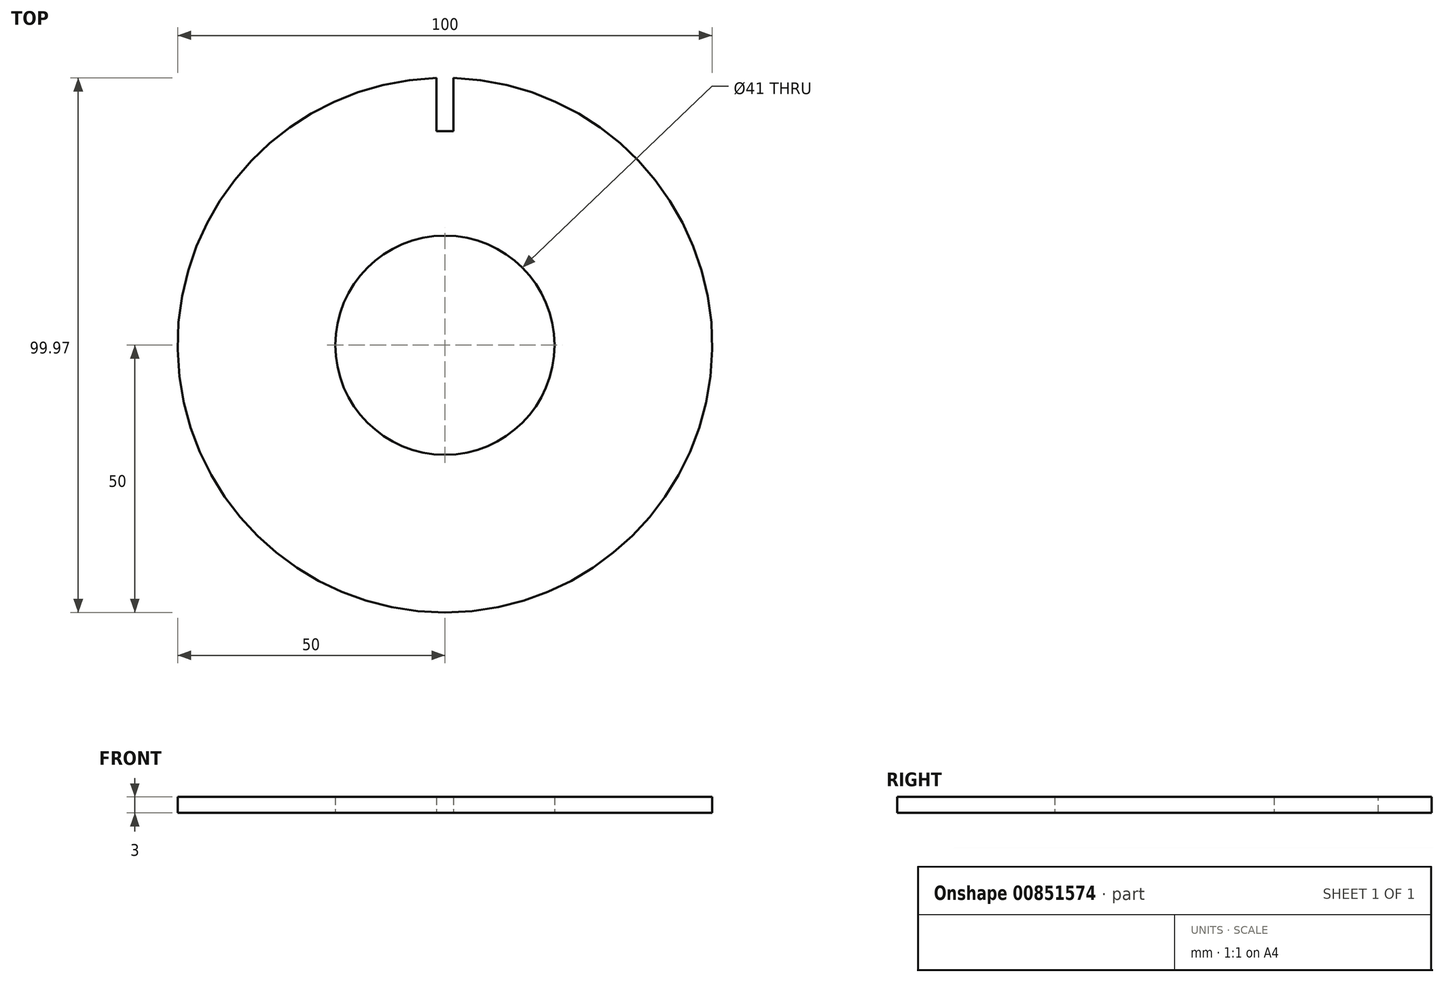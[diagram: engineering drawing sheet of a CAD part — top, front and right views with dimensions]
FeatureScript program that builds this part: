
annotation { "Feature Type Name" : "Feature", "Feature Type Description" : "" }
export const myFeature = defineFeature(function(context is Context, id is Id, definition is map)
    precondition{}
    {
        {
            var Q0;
            Q0=qCreatedBy(makeId("Top.planeOp"),FACE);
            var sketch = newSketch(context, id + "F0", { "sketchPlane" : qUnion([Q0])});
            skCircle(sketch, "E0", {"center": v(0, 0) * mm, "radius": 50 * mm});
            skCircle(sketch, "E1", {"center": v(0, 0) * mm, "radius": 20.5 * mm});
            skSolve(sketch);
        }
        {
            var Q0;
            Q0=qSketchRegion(id+"F0",true);
            extrude(context, id + "F1", {"entities" : qUnion([Q0]), "depth" : 3 * mm, "offsetDistance" : 25 * mm});
        }
        {
            var Q0;
            Q0=makeQuery(id+"F1.opExtrude","CAP_FACE",FACE,{"disambiguationData":[OSD([sQuery(id+"F0.wireOp",EDGE,"E0"),sQuery(id+"F0.wireOp",EDGE,"E1")])],"isStart":false});
            var sketch = newSketch(context, id + "F2", { "sketchPlane" : qUnion([Q0])});
            skLineSegment(sketch, "E2.bottom", {"start": v(-1.6, 80) * mm, "end": v(1.6, 80) * mm});
            skLineSegment(sketch, "E2.top", {"start": v(-1.6, 40) * mm, "end": v(1.6, 40) * mm});
            skLineSegment(sketch, "E2.left", {"start": v(-1.6, 80) * mm, "end": v(-1.6, 40) * mm});
            skLineSegment(sketch, "E2.right", {"start": v(1.6, 80) * mm, "end": v(1.6, 40) * mm});
            skLineSegment(sketch, "E3", {"start": v(0, 0) * mm, "end": v(0, 51.96) * mm, "construction": true});
            skSolve(sketch);
        }
        {
            var Q0;
            Q0=qSketchRegion(id+"F2",true);
            extrude(context, id + "F3", {"entities" : qUnion([Q0]), "operationType" : NewBodyOperationType.REMOVE, "oppositeDirection" : true, "depth" : 25 * mm});
        }
    });
